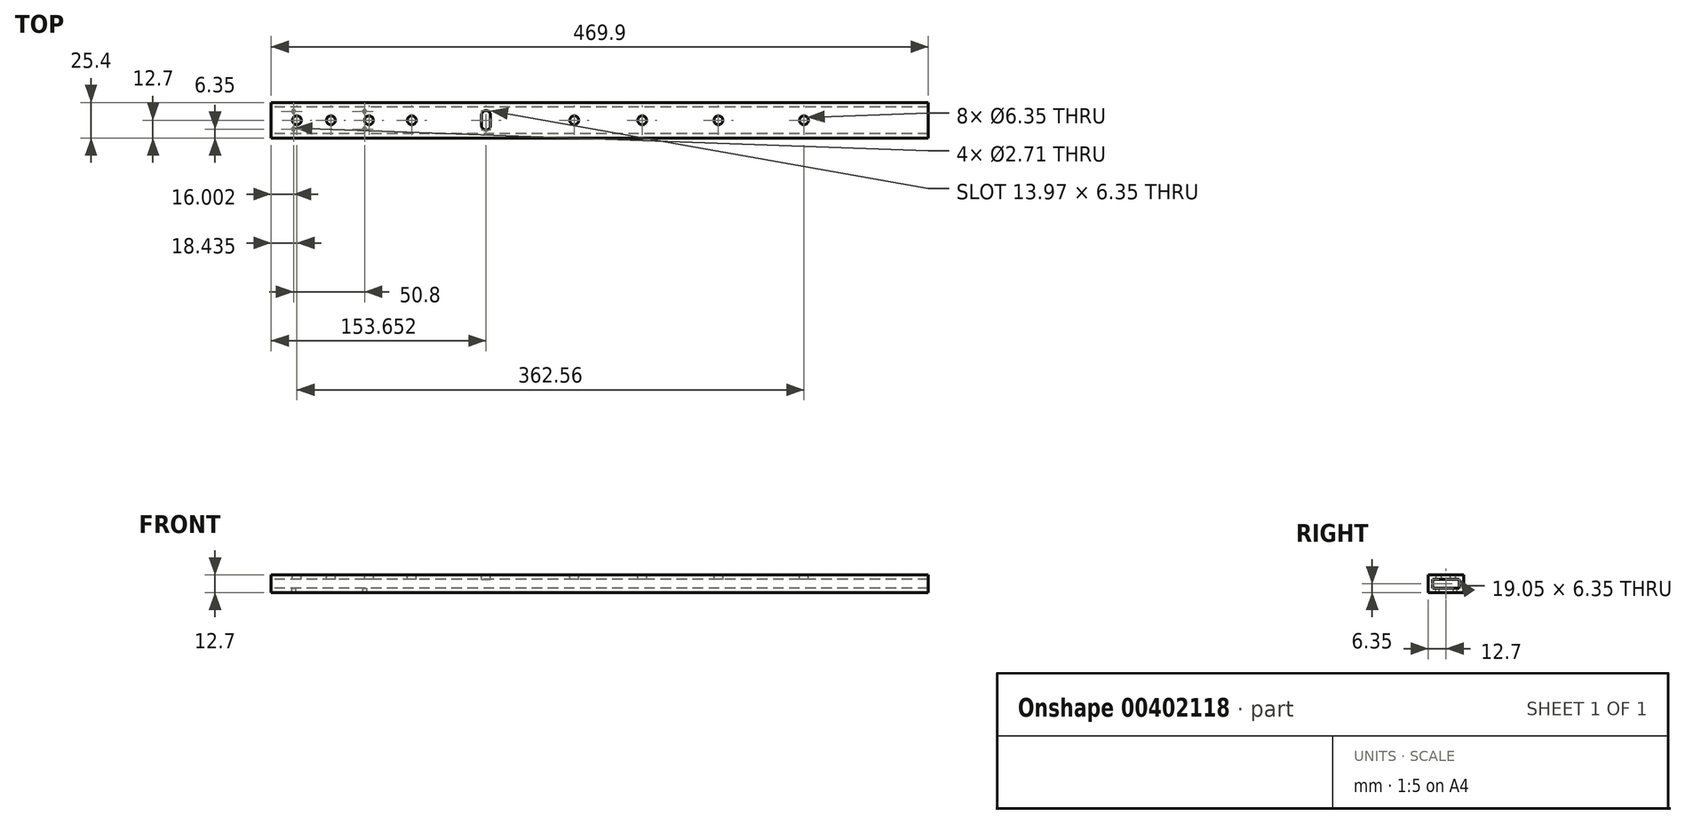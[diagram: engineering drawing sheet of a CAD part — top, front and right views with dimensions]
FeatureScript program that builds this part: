
annotation { "Feature Type Name" : "Feature", "Feature Type Description" : "" }
export const myFeature = defineFeature(function(context is Context, id is Id, definition is map)
    precondition{}
    {
        {
            var Q0;
            Q0=qCreatedBy(makeId("Right.planeOp"),FACE);
            var sketch = newSketch(context, id + "F0", { "sketchPlane" : qUnion([Q0])});
            skLineSegment(sketch, "E0.bottom", {"start": v(-12.7, 6.35) * mm, "end": v(12.7, 6.35) * mm});
            skLineSegment(sketch, "E0.top", {"start": v(-12.7, -6.35) * mm, "end": v(12.7, -6.35) * mm});
            skLineSegment(sketch, "E0.left", {"start": v(-12.7, 6.35) * mm, "end": v(-12.7, -6.35) * mm});
            skLineSegment(sketch, "E0.right", {"start": v(12.7, 6.35) * mm, "end": v(12.7, -6.35) * mm});
            skPoint(sketch, "E0.middle", {"position": v(0, 0) * mm});
            skLineSegment(sketch, "E1.bottom", {"start": v(-9.52, 3.18) * mm, "end": v(9.52, 3.18) * mm});
            skLineSegment(sketch, "E1.top", {"start": v(-9.52, -3.18) * mm, "end": v(9.52, -3.18) * mm});
            skLineSegment(sketch, "E1.left", {"start": v(-9.52, 3.18) * mm, "end": v(-9.52, -3.18) * mm});
            skLineSegment(sketch, "E1.right", {"start": v(9.52, 3.18) * mm, "end": v(9.52, -3.18) * mm});
            skSolve(sketch);
        }
        {
            var Q0;
            Q0=qSketchRegion(id+"F0",true);
            extrude(context, id + "F1", {"entities" : qUnion([Q0]), "depth" : 469.9 * mm});
        }
        {
            var Q0;
            Q0=makeQuery(id+"F1.opExtrude","SWEPT_FACE",FACE,{"disambiguationData":[OSD([sQuery(id+"F0.wireOp",EDGE,"E0.top")])]});
            var sketch = newSketch(context, id + "F2", { "sketchPlane" : qUnion([Q0])});
            skPoint(sketch, "E2", {"position": v(466.73, 6.35) * mm});
            skPoint(sketch, "E3", {"position": v(466.73, -6.35) * mm});
            skLineSegment(sketch, "E4", {"start": v(463.55, 0) * mm, "end": v(469.9, 0) * mm, "construction": true});
            skLineSegment(sketch, "E5", {"start": v(466.73, 0) * mm, "end": v(466.73, 6.35) * mm, "construction": true});
            skSolve(sketch);
        }
        {
            var Q0;
            Q0=makeQuery(id+"F1.opExtrude","SWEPT_FACE",FACE,{"disambiguationData":[OSD([sQuery(id+"F0.wireOp",EDGE,"E0.top")])]});
            var sketch = newSketch(context, id + "F3", { "sketchPlane" : qUnion([Q0])});
            skLineSegment(sketch, "E6", {"start": v(0, 0) * mm, "end": v(27.48, 0) * mm, "construction": true});
            skPoint(sketch, "E6.endSnap0", {"position": v(0, 0) * mm});
            skPoint(sketch, "E7", {"position": v(16, -6.35) * mm});
            skPoint(sketch, "E8", {"position": v(66.8, -6.35) * mm});
            skPoint(sketch, "E9", {"position": v(16, 6.35) * mm});
            skPoint(sketch, "E10", {"position": v(66.8, 6.35) * mm});
            skSolve(sketch);
        }
        {
            var Q0;
            Q0=sQuery(id+"F3.wireOp",VERTEX,"E7");
            var Q1;
            Q1=sQuery(id+"F3.wireOp",VERTEX,"E9");
            var Q2;
            Q2=sQuery(id+"F3.wireOp",VERTEX,"E10");
            var Q3;
            Q3=sQuery(id+"F3.wireOp",VERTEX,"E8");
            var Q4;
            Q4=makeQuery(id+"F1.opExtrude","SWEPT_BODY",BODY,{"disambiguationData":[OSD([sQuery(id+"F0.wireOp",EDGE,"E0.bottom"),sQuery(id+"F0.wireOp",EDGE,"E0.top"),sQuery(id+"F0.wireOp",EDGE,"E0.left"),sQuery(id+"F0.wireOp",EDGE,"E0.right"),sQuery(id+"F0.wireOp",EDGE,"E1.bottom"),sQuery(id+"F0.wireOp",EDGE,"E1.top"),sQuery(id+"F0.wireOp",EDGE,"E1.left"),sQuery(id+"F0.wireOp",EDGE,"E1.right")])]});
            hole(context, id + "F4", {"style" : HoleStyle.SIMPLE, "endStyle" : HoleEndStyle.BLIND, "standardTappedOrClearance" : lookupTablePath({ "standard" : "ANSI", "fit" : "Close (ASME)", "engagement" : "75%", "pitch" : "32 tpi", "size" : "#6", "type" : "Tapped" }), "standardBlindInLast" : lookupTablePath({ "fit" : "Close", "standard" : "ANSI", "engagement" : "75%", "pitch" : "32 tpi", "size" : "#6", "type" : "Tapped" }), "holeDiameter" : 2.7 * mm, "holeDepth" : 3.17 * mm, "locations" : qUnion([Q0, Q1, Q2, Q3]), "scope" : qUnion([Q4]), "majorDiameter" : 3.5 * mm});
        }
        {
            var Q0;
            Q0=makeQuery(id+"F1.opExtrude","SWEPT_FACE",FACE,{"disambiguationData":[OSD([sQuery(id+"F0.wireOp",EDGE,"E0.bottom")])]});
            var sketch = newSketch(context, id + "F5", { "sketchPlane" : qUnion([Q0])});
            skCircle(sketch, "E11", {"center": v(381, 0) * mm, "radius": 3.18 * mm});
            skCircle(sketch, "E12", {"center": v(319.82, 0) * mm, "radius": 3.18 * mm});
            skCircle(sketch, "E13", {"center": v(265.31, 0) * mm, "radius": 3.18 * mm});
            skCircle(sketch, "E14", {"center": v(216.75, 0) * mm, "radius": 3.18 * mm});
            skLineSegment(sketch, "E15", {"start": v(153.65, 0) * mm, "end": v(153.65, -3.8) * mm, "construction": true});
            skArc(sketch, "E16", {"start": v(150.48, -3.8) * mm, "mid": v(153.65, -6.98) * mm, "end": v(156.83, -3.8) * mm});
            skArc(sketch, "E17.MirrorC", {"start": v(150.48, 3.81) * mm, "mid": v(153.65, 6.99) * mm, "end": v(156.83, 3.81) * mm});
            skCircle(sketch, "E18", {"center": v(100.6, 0) * mm, "radius": 3.18 * mm});
            skCircle(sketch, "E19", {"center": v(69.98, 0) * mm, "radius": 3.18 * mm});
            skCircle(sketch, "E20", {"center": v(42.73, 0) * mm, "radius": 3.18 * mm});
            skCircle(sketch, "E21", {"center": v(18.43, 0) * mm, "radius": 3.18 * mm});
            skLineSegment(sketch, "E22", {"start": v(150.48, -3.8) * mm, "end": v(150.48, 3.81) * mm});
            skLineSegment(sketch, "E23", {"start": v(156.83, 3.81) * mm, "end": v(156.83, -3.8) * mm});
            skLineSegment(sketch, "E24", {"start": v(469.9, 0) * mm, "end": v(18.43, 0) * mm, "construction": true});
            skPoint(sketch, "E25", {"position": v(469.9, 0) * mm});
            skSolve(sketch);
        }
        {
            var Q0;
            Q0=qSketchRegion(id+"F5",true);
            extrude(context, id + "F6", {"entities" : qUnion([Q0]), "operationType" : NewBodyOperationType.REMOVE, "oppositeDirection" : true, "depth" : 3.17 * mm});
        }
    });
